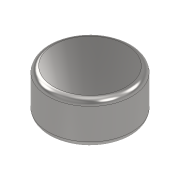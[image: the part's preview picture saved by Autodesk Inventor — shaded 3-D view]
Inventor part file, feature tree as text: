
AUTODESK INVENTOR PART (.ipt)
format: ipt  version: 2021 (Build 250183000, 183)  size: 120,832 bytes
history: native  units: mm
features: extrude x1, fillet x1, sketch x1
ambient origin geometry x8: Origin, YZ Plane, XZ Plane, XY Plane, X Axis, Y Axis, Z Axis, Center Point
bodies: Volumenkörper1 (feature_tree)
feature tree (3):
  extrude  "Extrusion1"  Depth=3.0mm TaperAngle=0.0deg
  fillet  "Rundung1"  Radius=0.4mm
  sketch  "Skizze1"  dims[d0=6.0mm d1=3.0mm d2=0.0mm d3=0.4mm]
